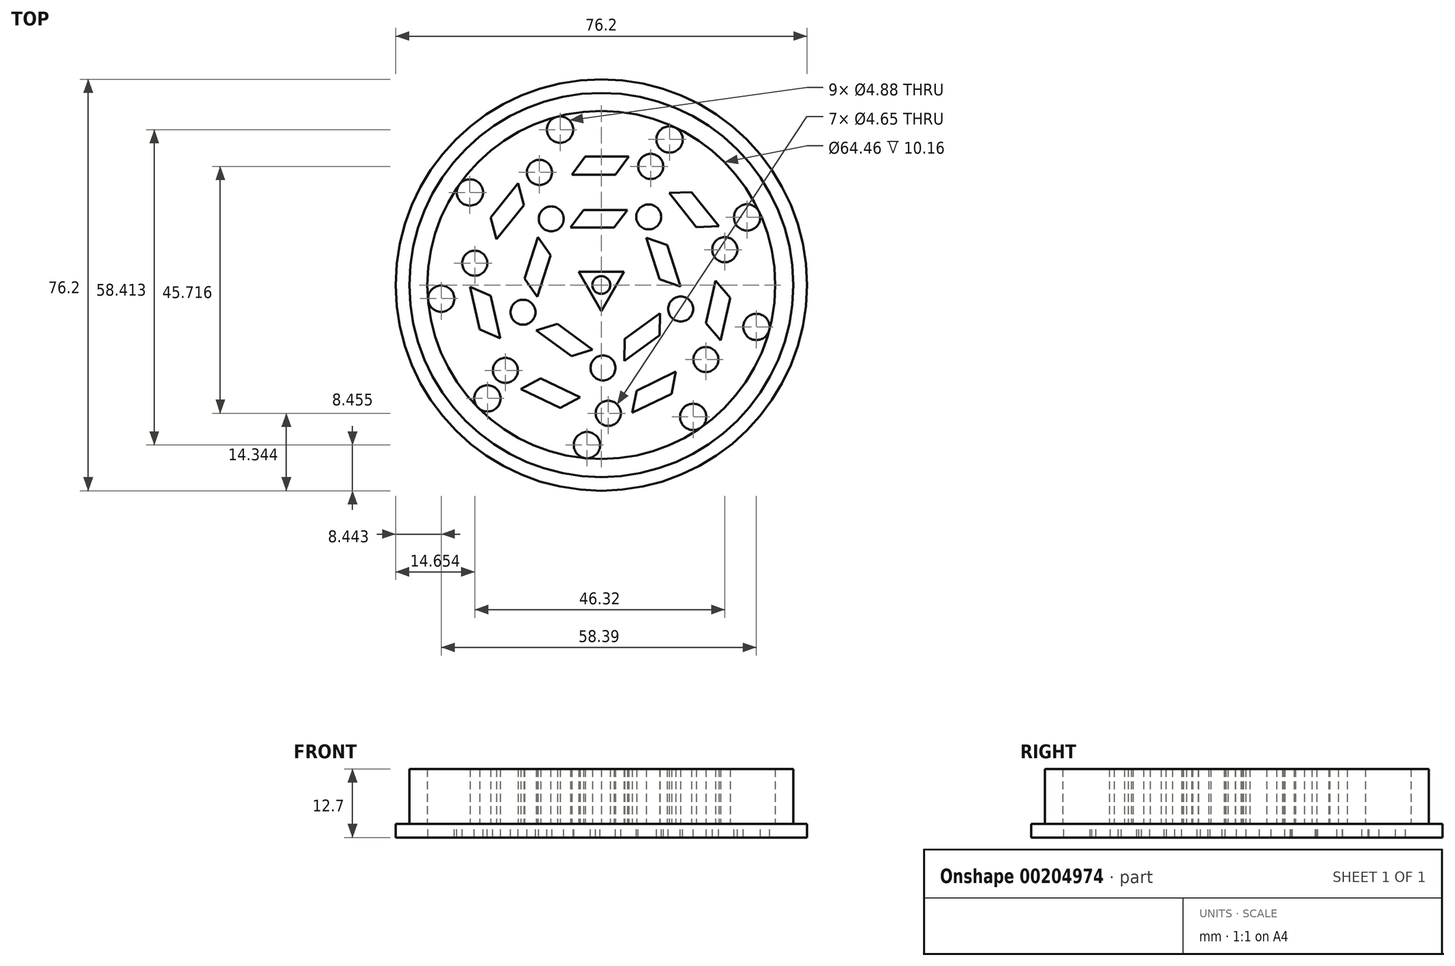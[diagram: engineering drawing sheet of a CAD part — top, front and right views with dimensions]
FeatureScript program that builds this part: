
annotation { "Feature Type Name" : "Feature", "Feature Type Description" : "" }
export const myFeature = defineFeature(function(context is Context, id is Id, definition is map)
    precondition{}
    {
        {
            var Q0;
            Q0=qCreatedBy(makeId("Top.planeOp"),FACE);
            var sketch = newSketch(context, id + "F0", { "sketchPlane" : qUnion([Q0])});
            skCircle(sketch, "E0", {"center": v(0, 0) * mm, "radius": 38.1 * mm});
            skSolve(sketch);
        }
        {
            var Q0;
            Q0=qCreatedBy(makeId("Top.planeOp"),FACE);
            var sketch = newSketch(context, id + "F1", { "sketchPlane" : qUnion([Q0])});
            skCircle(sketch, "E1", {"center": v(0, 0) * mm, "radius": 38.1 * mm});
            skCircle(sketch, "E2", {"center": v(0, 0) * mm, "radius": 35.56 * mm});
            skCircle(sketch, "E3", {"center": v(0, 0) * mm, "radius": 1.65 * mm});
            skCircle(sketch, "E4.cCircle", {"center": v(0, 0) * mm, "radius": 2.43 * mm, "construction": true});
            skLineSegment(sketch, "E4.0", {"start": v(4.21, 2.43) * mm, "end": v(0, -4.86) * mm});
            skLineSegment(sketch, "E4.1", {"start": v(0, -4.86) * mm, "end": v(-4.21, 2.43) * mm});
            skLineSegment(sketch, "E4.2", {"start": v(-4.21, 2.43) * mm, "end": v(4.21, 2.43) * mm});
            skPoint(sketch, "E4.0.midPoint", {"position": v(2.1, -1.22) * mm});
            skCircle(sketch, "E5", {"center": v(0, 0) * mm, "radius": 5.8 * mm, "construction": true});
            skCircle(sketch, "E6.0", {"center": v(0, 0) * mm, "radius": 9.86 * mm, "construction": true});
            skCircle(sketch, "E7.0", {"center": v(0, 0) * mm, "radius": 33.02 * mm});
            skCircle(sketch, "E8.0", {"center": v(0, 0) * mm, "radius": 10.62 * mm, "construction": true});
            skCircle(sketch, "E9.0", {"center": v(0, 0) * mm, "radius": 14.69 * mm, "construction": true});
            skLineSegment(sketch, "E10", {"start": v(4.81, 13.87) * mm, "end": v(-3.26, 13.87) * mm});
            skLineSegment(sketch, "E11", {"start": v(-3.26, 13.87) * mm, "end": v(-5.72, 10.62) * mm});
            skLineSegment(sketch, "E12", {"start": v(-5.72, 10.62) * mm, "end": v(2.36, 10.62) * mm});
            skLineSegment(sketch, "E13", {"start": v(2.36, 10.62) * mm, "end": v(4.81, 13.87) * mm});
            skLineSegment(sketch, "E14.1.0", {"start": v(-11.7, 8.86) * mm, "end": v(-14.2, 1.18) * mm});
            skLineSegment(sketch, "E14.1.1", {"start": v(-9.37, 5.53) * mm, "end": v(-11.7, 8.86) * mm});
            skLineSegment(sketch, "E14.1.2", {"start": v(-11.87, -2.16) * mm, "end": v(-9.37, 5.53) * mm});
            skLineSegment(sketch, "E14.1.3", {"start": v(-14.2, 1.18) * mm, "end": v(-11.87, -2.16) * mm});
            skLineSegment(sketch, "E14.2.0", {"start": v(-12.05, -8.4) * mm, "end": v(-5.51, -13.14) * mm});
            skLineSegment(sketch, "E14.2.1", {"start": v(-8.15, -7.2) * mm, "end": v(-12.05, -8.4) * mm});
            skLineSegment(sketch, "E14.2.2", {"start": v(-1.62, -11.95) * mm, "end": v(-8.15, -7.2) * mm});
            skLineSegment(sketch, "E14.2.3", {"start": v(-5.51, -13.14) * mm, "end": v(-1.62, -11.95) * mm});
            skLineSegment(sketch, "E14.3.0", {"start": v(4.26, -14.05) * mm, "end": v(10.8, -9.3) * mm});
            skLineSegment(sketch, "E14.3.1", {"start": v(4.33, -9.98) * mm, "end": v(4.26, -14.05) * mm});
            skLineSegment(sketch, "E14.3.2", {"start": v(10.87, -5.23) * mm, "end": v(4.33, -9.98) * mm});
            skLineSegment(sketch, "E14.3.3", {"start": v(10.8, -9.3) * mm, "end": v(10.87, -5.23) * mm});
            skLineSegment(sketch, "E14.4.0", {"start": v(14.68, -0.29) * mm, "end": v(12.19, 7.4) * mm});
            skLineSegment(sketch, "E14.4.1", {"start": v(10.83, 1.04) * mm, "end": v(14.68, -0.29) * mm});
            skLineSegment(sketch, "E14.4.2", {"start": v(8.33, 8.72) * mm, "end": v(10.83, 1.04) * mm});
            skLineSegment(sketch, "E14.4.3", {"start": v(12.19, 7.4) * mm, "end": v(8.33, 8.72) * mm});
            skCircle(sketch, "E15.0", {"center": v(0, 0) * mm, "radius": 15.45 * mm, "construction": true});
            skCircle(sketch, "E16.0", {"center": v(0, 0) * mm, "radius": 19.51 * mm, "construction": true});
            skCircle(sketch, "E17.0", {"center": v(0, 0) * mm, "radius": 20.27 * mm, "construction": true});
            skCircle(sketch, "E18.0", {"center": v(0, 0) * mm, "radius": 24.34 * mm, "construction": true});
            skLineSegment(sketch, "E19", {"start": v(5.08, 23.8) * mm, "end": v(-3, 23.8) * mm});
            skLineSegment(sketch, "E20", {"start": v(-3, 23.8) * mm, "end": v(-5.48, 20.45) * mm});
            skLineSegment(sketch, "E21", {"start": v(-5.48, 20.45) * mm, "end": v(2.6, 20.45) * mm});
            skLineSegment(sketch, "E22", {"start": v(2.6, 20.45) * mm, "end": v(5.08, 23.8) * mm});
            skLineSegment(sketch, "E23.1.0", {"start": v(-14.37, 14.78) * mm, "end": v(-15.45, 18.8) * mm});
            skLineSegment(sketch, "E23.1.1", {"start": v(-15.45, 18.8) * mm, "end": v(-20.48, 12.5) * mm});
            skLineSegment(sketch, "E23.1.2", {"start": v(-20.48, 12.5) * mm, "end": v(-19.4, 8.47) * mm});
            skLineSegment(sketch, "E23.1.3", {"start": v(-19.4, 8.47) * mm, "end": v(-14.37, 14.78) * mm});
            skLineSegment(sketch, "E23.2.0", {"start": v(-20.52, -2.02) * mm, "end": v(-24.33, -0.35) * mm});
            skLineSegment(sketch, "E23.2.1", {"start": v(-24.33, -0.35) * mm, "end": v(-22.54, -8.22) * mm});
            skLineSegment(sketch, "E23.2.2", {"start": v(-22.54, -8.22) * mm, "end": v(-18.72, -9.89) * mm});
            skLineSegment(sketch, "E23.2.3", {"start": v(-18.72, -9.89) * mm, "end": v(-20.52, -2.02) * mm});
            skLineSegment(sketch, "E23.3.0", {"start": v(-11.22, -17.3) * mm, "end": v(-14.9, -19.24) * mm});
            skLineSegment(sketch, "E23.3.1", {"start": v(-14.9, -19.24) * mm, "end": v(-7.62, -22.75) * mm});
            skLineSegment(sketch, "E23.3.2", {"start": v(-7.62, -22.75) * mm, "end": v(-3.94, -20.8) * mm});
            skLineSegment(sketch, "E23.3.3", {"start": v(-3.94, -20.8) * mm, "end": v(-11.22, -17.3) * mm});
            skLineSegment(sketch, "E23.4.0", {"start": v(6.53, -19.55) * mm, "end": v(5.75, -23.65) * mm});
            skLineSegment(sketch, "E23.4.1", {"start": v(5.75, -23.65) * mm, "end": v(13.03, -20.14) * mm});
            skLineSegment(sketch, "E23.4.2", {"start": v(13.03, -20.14) * mm, "end": v(13.8, -16.05) * mm});
            skLineSegment(sketch, "E23.4.3", {"start": v(13.8, -16.05) * mm, "end": v(6.53, -19.55) * mm});
            skLineSegment(sketch, "E23.5.0", {"start": v(19.36, -7.09) * mm, "end": v(22.08, -10.24) * mm});
            skLineSegment(sketch, "E23.5.1", {"start": v(22.08, -10.24) * mm, "end": v(23.87, -2.37) * mm});
            skLineSegment(sketch, "E23.5.2", {"start": v(23.87, -2.37) * mm, "end": v(21.16, 0.79) * mm});
            skLineSegment(sketch, "E23.5.3", {"start": v(21.16, 0.79) * mm, "end": v(19.36, -7.09) * mm});
            skLineSegment(sketch, "E23.6.0", {"start": v(17.61, 10.72) * mm, "end": v(21.77, 10.87) * mm});
            skLineSegment(sketch, "E23.6.1", {"start": v(21.77, 10.87) * mm, "end": v(16.74, 17.19) * mm});
            skLineSegment(sketch, "E23.6.2", {"start": v(16.74, 17.19) * mm, "end": v(12.58, 17.03) * mm});
            skLineSegment(sketch, "E23.6.3", {"start": v(12.58, 17.03) * mm, "end": v(17.61, 10.72) * mm});
            skCircle(sketch, "E24.0", {"center": v(0, 0) * mm, "radius": 25.1 * mm, "construction": true});
            skCircle(sketch, "E25.0", {"center": v(0, 0) * mm, "radius": 29.16 * mm, "construction": true});
            skCircle(sketch, "E26.0", {"center": v(0, 0) * mm, "radius": 29.93 * mm, "construction": true});
            skLineSegment(sketch, "E27", {"start": v(7.1, 32.25) * mm, "end": v(4.61, 29.57) * mm});
            skLineSegment(sketch, "E28", {"start": v(4.61, 29.57) * mm, "end": v(-3.8, 29.68) * mm});
            skLineSegment(sketch, "E29", {"start": v(-3.8, 29.68) * mm, "end": v(-5.56, 32.55) * mm});
            skLineSegment(sketch, "E30.1.0", {"start": v(-15.3, 29.26) * mm, "end": v(-15.47, 25.61) * mm});
            skLineSegment(sketch, "E30.1.1", {"start": v(-15.47, 25.61) * mm, "end": v(-22, 20.29) * mm});
            skLineSegment(sketch, "E30.1.2", {"start": v(-22, 20.29) * mm, "end": v(-25.18, 21.36) * mm});
            skLineSegment(sketch, "E30.2.0", {"start": v(-30.53, 12.59) * mm, "end": v(-28.32, 9.67) * mm});
            skLineSegment(sketch, "E30.2.1", {"start": v(-28.32, 9.67) * mm, "end": v(-29.9, 1.4) * mm});
            skLineSegment(sketch, "E30.2.2", {"start": v(-29.9, 1.4) * mm, "end": v(-33.02, 0.18) * mm});
            skLineSegment(sketch, "E30.3.0", {"start": v(-31.48, -9.98) * mm, "end": v(-27.91, -10.8) * mm});
            skLineSegment(sketch, "E30.3.1", {"start": v(-27.91, -10.8) * mm, "end": v(-23.8, -18.14) * mm});
            skLineSegment(sketch, "E30.3.2", {"start": v(-23.8, -18.14) * mm, "end": v(-25.4, -21.09) * mm});
            skLineSegment(sketch, "E30.4.0", {"start": v(-17.7, -27.88) * mm, "end": v(-14.45, -26.2) * mm});
            skLineSegment(sketch, "E30.4.1", {"start": v(-14.45, -26.2) * mm, "end": v(-6.57, -29.2) * mm});
            skLineSegment(sketch, "E30.4.2", {"start": v(-6.57, -29.2) * mm, "end": v(-5.9, -32.49) * mm});
            skLineSegment(sketch, "E30.5.0", {"start": v(4.36, -32.73) * mm, "end": v(5.78, -29.36) * mm});
            skLineSegment(sketch, "E30.5.1", {"start": v(5.78, -29.36) * mm, "end": v(13.73, -26.59) * mm});
            skLineSegment(sketch, "E30.5.2", {"start": v(13.73, -26.59) * mm, "end": v(16.36, -28.68) * mm});
            skLineSegment(sketch, "E30.6.0", {"start": v(24.38, -22.27) * mm, "end": v(23.3, -18.78) * mm});
            skLineSegment(sketch, "E30.6.1", {"start": v(23.3, -18.78) * mm, "end": v(27.61, -11.54) * mm});
            skLineSegment(sketch, "E30.6.2", {"start": v(27.61, -11.54) * mm, "end": v(30.97, -11.46) * mm});
            skLineSegment(sketch, "E30.7.0", {"start": v(33, -1.39) * mm, "end": v(29.92, 0.6) * mm});
            skLineSegment(sketch, "E30.7.1", {"start": v(29.92, 0.6) * mm, "end": v(28.57, 8.9) * mm});
            skLineSegment(sketch, "E30.7.2", {"start": v(28.57, 8.9) * mm, "end": v(31.09, 11.13) * mm});
            skLineSegment(sketch, "E30.8.0", {"start": v(26.16, 20.14) * mm, "end": v(22.54, 19.69) * mm});
            skLineSegment(sketch, "E30.8.1", {"start": v(22.54, 19.69) * mm, "end": v(16.16, 25.19) * mm});
            skLineSegment(sketch, "E30.8.2", {"start": v(16.16, 25.19) * mm, "end": v(16.66, 28.5) * mm});
            skSolve(sketch);
        }
        {
            var Q0;
            Q0 = qSketchRegion(id + "F0", true);
            extrude(context, id + "F2", {"entities" : qUnion([Q0]), "oppositeDirection" : true, "depth" : 2.54 * mm});
        }
        {
            var Q0;
            Q0=makeQuery(id+"F1.imprint","IMPRINT",FACE,{"disambiguationData":[TD([[makeQuery(id+"F1.imprint","IMPRINT",EDGE,{"derivedFrom":sQuery(id+"F1.wireOp",EDGE,"E2")}),1.0]])]});
            var Q1;
            Q1=makeQuery(id+"F1.imprint","IMPRINT",FACE,{"disambiguationData":[TD([[makeQuery(id+"F1.imprint","IMPRINT",EDGE,{"derivedFrom":sQuery(id+"F1.wireOp",EDGE,"E19")}),1.0]])]});
            var Q2;
            Q2=makeQuery(id+"F1.imprint","IMPRINT",FACE,{"disambiguationData":[TD([[makeQuery(id+"F1.imprint","IMPRINT",EDGE,{"derivedFrom":sQuery(id+"F1.wireOp",EDGE,"E23.6.0")}),1.0]])]});
            var Q3;
            Q3=makeQuery(id+"F1.imprint","IMPRINT",FACE,{"disambiguationData":[TD([[makeQuery(id+"F1.imprint","IMPRINT",EDGE,{"derivedFrom":sQuery(id+"F1.wireOp",EDGE,"E23.5.0")}),1.0]])]});
            var Q4;
            Q4=makeQuery(id+"F1.imprint","IMPRINT",FACE,{"disambiguationData":[TD([[makeQuery(id+"F1.imprint","IMPRINT",EDGE,{"derivedFrom":sQuery(id+"F1.wireOp",EDGE,"E23.4.0")}),1.0]])]});
            var Q5;
            Q5=makeQuery(id+"F1.imprint","IMPRINT",FACE,{"disambiguationData":[TD([[makeQuery(id+"F1.imprint","IMPRINT",EDGE,{"derivedFrom":sQuery(id+"F1.wireOp",EDGE,"E23.3.0")}),1.0]])]});
            var Q6;
            Q6=makeQuery(id+"F1.imprint","IMPRINT",FACE,{"disambiguationData":[TD([[makeQuery(id+"F1.imprint","IMPRINT",EDGE,{"derivedFrom":sQuery(id+"F1.wireOp",EDGE,"E23.2.0")}),1.0]])]});
            var Q7;
            Q7=makeQuery(id+"F1.imprint","IMPRINT",FACE,{"disambiguationData":[TD([[makeQuery(id+"F1.imprint","IMPRINT",EDGE,{"derivedFrom":sQuery(id+"F1.wireOp",EDGE,"E23.1.0")}),1.0]])]});
            var Q8;
            Q8=makeQuery(id+"F1.imprint","IMPRINT",FACE,{"disambiguationData":[TD([[makeQuery(id+"F1.imprint","IMPRINT",EDGE,{"derivedFrom":sQuery(id+"F1.wireOp",EDGE,"E10")}),1.0]])]});
            var Q9;
            Q9=makeQuery(id+"F1.imprint","IMPRINT",FACE,{"disambiguationData":[TD([[makeQuery(id+"F1.imprint","IMPRINT",EDGE,{"derivedFrom":sQuery(id+"F1.wireOp",EDGE,"E14.4.0")}),1.0]])]});
            var Q10;
            Q10=makeQuery(id+"F1.imprint","IMPRINT",FACE,{"disambiguationData":[TD([[makeQuery(id+"F1.imprint","IMPRINT",EDGE,{"derivedFrom":sQuery(id+"F1.wireOp",EDGE,"E14.3.0")}),1.0]])]});
            var Q11;
            Q11=makeQuery(id+"F1.imprint","IMPRINT",FACE,{"disambiguationData":[TD([[makeQuery(id+"F1.imprint","IMPRINT",EDGE,{"derivedFrom":sQuery(id+"F1.wireOp",EDGE,"E14.2.0")}),1.0]])]});
            var Q12;
            Q12=makeQuery(id+"F1.imprint","IMPRINT",FACE,{"disambiguationData":[TD([[makeQuery(id+"F1.imprint","IMPRINT",EDGE,{"derivedFrom":sQuery(id+"F1.wireOp",EDGE,"E14.1.0")}),1.0]])]});
            var Q13;
            Q13=makeQuery(id+"F1.imprint","IMPRINT",FACE,{"disambiguationData":[TD([[makeQuery(id+"F1.imprint","IMPRINT",EDGE,{"derivedFrom":sQuery(id+"F1.wireOp",EDGE,"E3")}),-1.0]])]});
            extrude(context, id + "F3", {"entities" : qUnion([Q0, Q1, Q2, Q3, Q4, Q5, Q6, Q7, Q8, Q9, Q10, Q11, Q12, Q13]), "operationType" : NewBodyOperationType.ADD, "depth" : 10.16 * mm});
        }
        {
            var Q0;
            Q0=makeQuery(id+"F3.boolean.opBoolean","SPLIT",FACE,{"disambiguationData":[TD([makeQuery(id+"F3.opExtrude","SWEPT_FACE",FACE,{"disambiguationData":[OSD([sQuery(id+"F1.wireOp",EDGE,"E4.0")])]})])],"derivedFrom":makeQuery(id+"F2.opExtrude","CAP_FACE",FACE,{"disambiguationData":[OSD([sQuery(id+"F0.wireOp",EDGE,"E0")])],"isStart":true})});
            var sketch = newSketch(context, id + "F4", { "sketchPlane" : qUnion([Q0])});
            skCircle(sketch, "E31", {"center": v(-7.64, 28.77) * mm, "radius": 2.44 * mm});
            skCircle(sketch, "E32.1.0", {"center": v(-24.34, 17.13) * mm, "radius": 2.44 * mm});
            skCircle(sketch, "E32.2.0", {"center": v(-29.66, -2.53) * mm, "radius": 2.44 * mm});
            skCircle(sketch, "E32.3.0", {"center": v(-21.1, -21) * mm, "radius": 2.44 * mm});
            skCircle(sketch, "E32.4.0", {"center": v(-2.66, -29.65) * mm, "radius": 2.44 * mm});
            skCircle(sketch, "E32.5.0", {"center": v(17.02, -24.42) * mm, "radius": 2.44 * mm});
            skCircle(sketch, "E32.6.0", {"center": v(28.73, -7.77) * mm, "radius": 2.44 * mm});
            skCircle(sketch, "E32.7.0", {"center": v(27, 12.52) * mm, "radius": 2.44 * mm});
            skCircle(sketch, "E32.8.0", {"center": v(12.64, 26.95) * mm, "radius": 2.44 * mm});
            skPoint(sketch, "E32.center", {"position": v(0, 0) * mm});
            skCircle(sketch, "E33", {"center": v(-11.46, 20.85) * mm, "radius": 2.33 * mm});
            skCircle(sketch, "E34.1.0", {"center": v(-23.45, 4.04) * mm, "radius": 2.33 * mm});
            skCircle(sketch, "E34.2.0", {"center": v(-17.77, -15.81) * mm, "radius": 2.33 * mm});
            skCircle(sketch, "E34.3.0", {"center": v(1.28, -23.76) * mm, "radius": 2.33 * mm});
            skCircle(sketch, "E34.4.0", {"center": v(19.37, -13.8) * mm, "radius": 2.33 * mm});
            skCircle(sketch, "E34.5.0", {"center": v(22.87, 6.54) * mm, "radius": 2.33 * mm});
            skCircle(sketch, "E34.6.0", {"center": v(9.15, 21.96) * mm, "radius": 2.33 * mm});
            skCircle(sketch, "E35", {"center": v(-9.28, 12.24) * mm, "radius": 2.3 * mm});
            skCircle(sketch, "E36.1.0", {"center": v(-14.51, -5.04) * mm, "radius": 2.3 * mm});
            skCircle(sketch, "E36.2.0", {"center": v(0.3, -15.36) * mm, "radius": 2.3 * mm});
            skCircle(sketch, "E36.3.0", {"center": v(14.7, -4.45) * mm, "radius": 2.3 * mm});
            skCircle(sketch, "E36.4.0", {"center": v(8.78, 12.6) * mm, "radius": 2.3 * mm});
            skSolve(sketch);
        }
        {
            var Q0;
            Q0 = qSketchRegion(id + "F4", true);
            extrude(context, id + "F5", {"entities" : qUnion([Q0]), "operationType" : NewBodyOperationType.REMOVE, "endBound" : BoundingType.THROUGH_ALL, "oppositeDirection" : true, "depth" : 25.4 * mm});
        }
        {
            var Q0;
            Q0=makeQuery(id+"F3.boolean.opBoolean","SPLIT",FACE,{"disambiguationData":[TD([makeQuery(id+"F3.opExtrude","SWEPT_FACE",FACE,{"disambiguationData":[OSD([sQuery(id+"F1.wireOp",EDGE,"E4.0")])]})])],"derivedFrom":makeQuery(id+"F2.opExtrude","CAP_FACE",FACE,{"disambiguationData":[OSD([sQuery(id+"F0.wireOp",EDGE,"E0")])],"isStart":true})});
            var sketch = newSketch(context, id + "F6", { "sketchPlane" : qUnion([Q0])});
            skCircle(sketch, "E37", {"center": v(0, 0) * mm, "radius": 32.23 * mm});
            skCircle(sketch, "E38", {"center": v(0, 0) * mm, "radius": 34.94 * mm});
            skSolve(sketch);
        }
        {
            var Q0;
            Q0=makeQuery(id+"F6.imprint","IMPRINT",FACE,{"disambiguationData":[TD([[makeQuery(id+"F6.imprint","IMPRINT",EDGE,{"derivedFrom":makeQuery(id+"F3.opExtrude","CAP_EDGE",EDGE,{"disambiguationData":[OSD([sQuery(id+"F1.wireOp",EDGE,"E7.0")])],"isStart":true})}),1.0]])]});
            var Q1;
            Q1=makeQuery(id+"F3.opExtrude","CAP_FACE",FACE,{"disambiguationData":[OSD([sQuery(id+"F1.wireOp",EDGE,"E2"),sQuery(id+"F1.wireOp",EDGE,"E7.0")])],"isStart":false});
            extrude(context, id + "F7", {"entities" : qUnion([Q0]), "operationType" : NewBodyOperationType.ADD, "endBound" : BoundingType.UP_TO_SURFACE, "endBoundEntityFace" : qUnion([Q1]), "depth" : 25.4 * mm});
        }
    });
